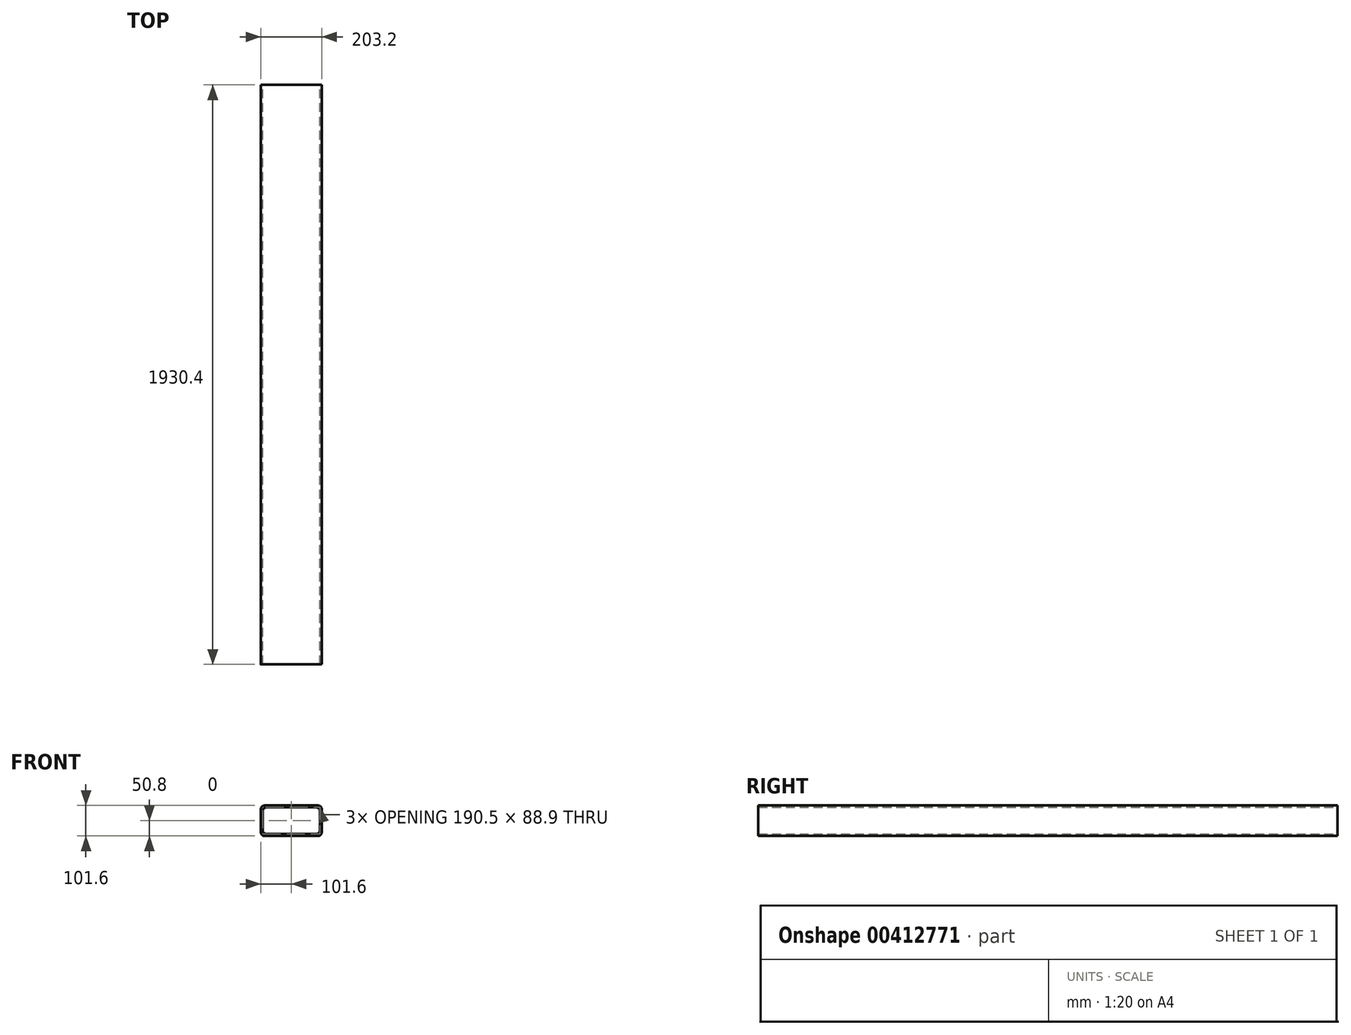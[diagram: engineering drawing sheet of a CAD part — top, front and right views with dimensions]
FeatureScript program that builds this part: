
annotation { "Feature Type Name" : "Feature", "Feature Type Description" : "" }
export const myFeature = defineFeature(function(context is Context, id is Id, definition is map)
    precondition{}
    {
        {
            var Q0;
            Q0=qCreatedBy(makeId("Front.planeOp"),FACE);
            var sketch = newSketch(context, id + "F0", { "sketchPlane" : qUnion([Q0])});
            skLineSegment(sketch, "E0.bottom", {"start": v(12.7, 0) * mm, "end": v(190.5, 0) * mm});
            skLineSegment(sketch, "E0.top", {"start": v(12.7, 101.6) * mm, "end": v(190.5, 101.6) * mm});
            skLineSegment(sketch, "E0.left", {"start": v(0, 12.7) * mm, "end": v(0, 88.9) * mm});
            skLineSegment(sketch, "E0.right", {"start": v(203.2, 12.7) * mm, "end": v(203.2, 88.9) * mm});
            skLineSegment(sketch, "E1.bottom", {"start": v(19.05, 6.35) * mm, "end": v(184.15, 6.35) * mm});
            skLineSegment(sketch, "E1.top", {"start": v(19.05, 95.25) * mm, "end": v(184.15, 95.25) * mm});
            skLineSegment(sketch, "E1.left", {"start": v(6.35, 19.05) * mm, "end": v(6.35, 82.55) * mm});
            skLineSegment(sketch, "E1.right", {"start": v(196.85, 19.05) * mm, "end": v(196.85, 82.55) * mm});
            skPoint(sketch, "E2.visualSharp", {"position": v(0, 101.6) * mm});
            skArc(sketch, "E2.filletArc", {"start": v(12.7, 101.6) * mm, "mid": v(3.72, 97.88) * mm, "end": v(0, 88.9) * mm});
            skPoint(sketch, "E3.visualSharp", {"position": v(203.2, 101.6) * mm});
            skArc(sketch, "E3.filletArc", {"start": v(203.2, 88.9) * mm, "mid": v(199.48, 97.88) * mm, "end": v(190.5, 101.6) * mm});
            skPoint(sketch, "E4.visualSharp", {"position": v(196.85, 95.25) * mm});
            skArc(sketch, "E4.filletArc", {"start": v(196.85, 82.55) * mm, "mid": v(193.13, 91.53) * mm, "end": v(184.15, 95.25) * mm});
            skPoint(sketch, "E5.visualSharp", {"position": v(196.85, 6.35) * mm});
            skArc(sketch, "E5.filletArc", {"start": v(184.15, 6.35) * mm, "mid": v(193.13, 10.07) * mm, "end": v(196.85, 19.05) * mm});
            skPoint(sketch, "E6.visualSharp", {"position": v(203.2, 0) * mm});
            skArc(sketch, "E6.filletArc", {"start": v(190.5, 0) * mm, "mid": v(199.48, 3.72) * mm, "end": v(203.2, 12.7) * mm});
            skPoint(sketch, "E7.visualSharp", {"position": v(6.35, 6.35) * mm});
            skArc(sketch, "E7.filletArc", {"start": v(6.35, 19.05) * mm, "mid": v(10.07, 10.07) * mm, "end": v(19.05, 6.35) * mm});
            skPoint(sketch, "E8.visualSharp", {"position": v(0, 0) * mm});
            skArc(sketch, "E8.filletArc", {"start": v(0, 12.7) * mm, "mid": v(3.72, 3.72) * mm, "end": v(12.7, 0) * mm});
            skPoint(sketch, "E9.visualSharp", {"position": v(6.35, 95.25) * mm});
            skArc(sketch, "E9.filletArc", {"start": v(19.05, 95.25) * mm, "mid": v(10.07, 91.53) * mm, "end": v(6.35, 82.55) * mm});
            skSolve(sketch);
        }
        {
            var Q0;
            Q0 = qSketchRegion(id + "F0", true);
            extrude(context, id + "F1", {"entities" : qUnion([Q0]), "depth" : 1930.4 * mm, "offsetDistance" : 25.4 * mm});
        }
    });
